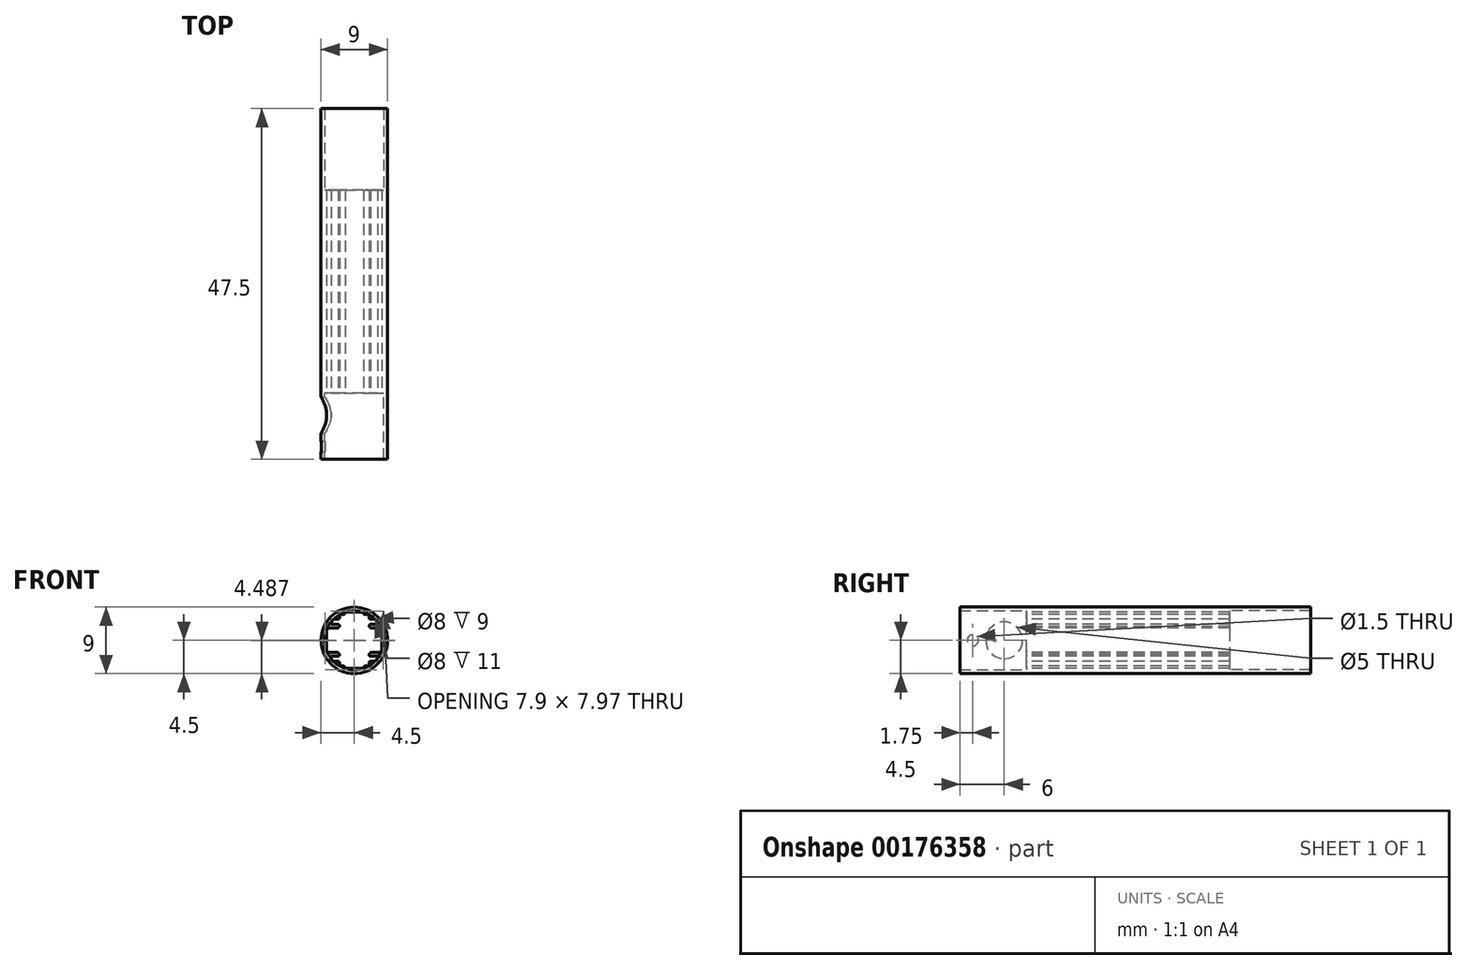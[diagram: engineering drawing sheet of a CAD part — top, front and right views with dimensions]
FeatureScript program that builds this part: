
annotation { "Feature Type Name" : "Feature", "Feature Type Description" : "" }
export const myFeature = defineFeature(function(context is Context, id is Id, definition is map)
    precondition{}
    {
        {
            assignVariable(context, id + "F0", {"name" : "Main_Length", "anyValue" : 47.5});
        }
        {
            assignVariable(context, id + "F1", {"name" : "Bore_Depth_F", "anyValue" : 9});
        }
        {
            assignVariable(context, id + "F2", {"name" : "Bore_Depth_R", "anyValue" : 11});
        }
        {
            var Q0;
            Q0=qCreatedBy(makeId("Front.planeOp"),FACE);
            var sketch = newSketch(context, id + "F3", { "sketchPlane" : qUnion([Q0])});
            skCircle(sketch, "E0", {"center": v(0, 0) * mm, "radius": 4.5 * mm});
            skSolve(sketch);
        }
        {
            var Q0;
            Q0=makeQuery(id+"F3.imprint","IMPRINT",FACE,{"disambiguationData":[TD([[makeQuery(id+"F3.imprint","IMPRINT",EDGE,{"derivedFrom":sQuery(id+"F3.wireOp",EDGE,"E0")}),1.0]])]});
            extrude(context, id + "F4", {"entities" : qUnion([Q0]), "depth" : (getVariable(context, 'Main_Length') - getVariable(context, 'Bore_Depth_F') - getVariable(context, 'Bore_Depth_R')) * mm});
        }
        {
            var Q0;
            Q0=makeQuery(id+"F4.opExtrude","CAP_FACE",FACE,{"disambiguationData":[OSD([sQuery(id+"F3.wireOp",EDGE,"E0")])],"isStart":false});
            var sketch = newSketch(context, id + "F5", { "sketchPlane" : qUnion([Q0])});
            skLineSegment(sketch, "E1", {"start": v(0, -3.8) * mm, "end": v(1.25, -3.8) * mm});
            skLineSegment(sketch, "E2", {"start": v(3.75, -1.65) * mm, "end": v(3.75, 0) * mm});
            skLineSegment(sketch, "E3", {"start": v(1.45, -3.5) * mm, "end": v(2, -3.5) * mm});
            skLineSegment(sketch, "E4", {"start": v(3.15, 2.15) * mm, "end": v(2.2, 2.15) * mm});
            skLineSegment(sketch, "E5", {"start": v(2, -1.95) * mm, "end": v(2, -1.89) * mm});
            skLineSegment(sketch, "E6", {"start": v(1.25, -3.8) * mm, "end": v(1.25, -3.7) * mm});
            skArc(sketch, "E7", {"start": v(2, -1.95) * mm, "mid": v(2.06, -2.1) * mm, "end": v(2.2, -2.15) * mm});
            skArc(sketch, "E8", {"start": v(1.45, -3.5) * mm, "mid": v(1.3, -3.56) * mm, "end": v(1.25, -3.7) * mm});
            skArc(sketch, "E9", {"start": v(2.2, 2.85) * mm, "mid": v(2.06, 2.9) * mm, "end": v(2, 3.05) * mm});
            skArc(sketch, "E10", {"start": v(2, 1.95) * mm, "mid": v(2.06, 2.1) * mm, "end": v(2.2, 2.15) * mm});
            skArc(sketch, "E11", {"start": v(2.2, -2.85) * mm, "mid": v(2.06, -2.9) * mm, "end": v(2, -3.05) * mm});
            skLineSegment(sketch, "E12", {"start": v(1.25, 3.8) * mm, "end": v(1.25, 3.7) * mm});
            skLineSegment(sketch, "E13", {"start": v(-3.75, -1.65) * mm, "end": v(-3.75, 0) * mm});
            skLineSegment(sketch, "E14", {"start": v(-3.15, -2.15) * mm, "end": v(-2.2, -2.15) * mm});
            skLineSegment(sketch, "E15", {"start": v(-3.15, -2.85) * mm, "end": v(-3.15, -2.15) * mm});
            skLineSegment(sketch, "E16", {"start": v(-2.2, -2.85) * mm, "end": v(-3.15, -2.85) * mm});
            skLineSegment(sketch, "E17", {"start": v(-2, -3.5) * mm, "end": v(-2, -3.05) * mm});
            skArc(sketch, "E18", {"start": v(-2.2, -2.85) * mm, "mid": v(-2.06, -2.9) * mm, "end": v(-2, -3.05) * mm});
            skLineSegment(sketch, "E19", {"start": v(-2, -1.95) * mm, "end": v(-2, -1.89) * mm});
            skLineSegment(sketch, "E20", {"start": v(-1.25, -3.8) * mm, "end": v(-1.25, -3.7) * mm});
            skArc(sketch, "E21", {"start": v(-1.45, 3.5) * mm, "mid": v(-1.3, 3.56) * mm, "end": v(-1.25, 3.7) * mm});
            skLineSegment(sketch, "E22", {"start": v(-3.15, 2.15) * mm, "end": v(-2.2, 2.15) * mm});
            skLineSegment(sketch, "E23", {"start": v(2.2, -2.85) * mm, "end": v(3.15, -2.85) * mm});
            skLineSegment(sketch, "E24", {"start": v(2.2, -1.65) * mm, "end": v(3.75, -1.65) * mm});
            skLineSegment(sketch, "E25", {"start": v(-2.2, 2.85) * mm, "end": v(-3.15, 2.85) * mm});
            skLineSegment(sketch, "E26", {"start": v(-1.45, 3.5) * mm, "end": v(-2, 3.5) * mm});
            skLineSegment(sketch, "E27", {"start": v(0, 3.8) * mm, "end": v(-1.25, 3.8) * mm});
            skLineSegment(sketch, "E28", {"start": v(3.15, -2.85) * mm, "end": v(3.15, -2.15) * mm});
            skLineSegment(sketch, "E29", {"start": v(-1.45, -3.5) * mm, "end": v(-2, -3.5) * mm});
            skLineSegment(sketch, "E30", {"start": v(-2, 3.5) * mm, "end": v(-2, 3.05) * mm});
            skArc(sketch, "E31", {"start": v(-1.45, -3.5) * mm, "mid": v(-1.3, -3.56) * mm, "end": v(-1.25, -3.7) * mm});
            skArc(sketch, "E32", {"start": v(-2, 1.95) * mm, "mid": v(-2.06, 2.1) * mm, "end": v(-2.2, 2.15) * mm});
            skArc(sketch, "E33", {"start": v(2, -1.89) * mm, "mid": v(2.1, -1.77) * mm, "end": v(2.2, -1.65) * mm});
            skLineSegment(sketch, "E34", {"start": v(2.2, 1.65) * mm, "end": v(3.75, 1.65) * mm});
            skLineSegment(sketch, "E35", {"start": v(3.15, 2.85) * mm, "end": v(3.15, 2.15) * mm});
            skLineSegment(sketch, "E36", {"start": v(2, -3.5) * mm, "end": v(2, -3.05) * mm});
            skLineSegment(sketch, "E37", {"start": v(-2.2, -1.65) * mm, "end": v(-3.75, -1.65) * mm});
            skLineSegment(sketch, "E38", {"start": v(-3.75, 1.65) * mm, "end": v(-3.75, 0) * mm});
            skLineSegment(sketch, "E39", {"start": v(0, -3.8) * mm, "end": v(-1.25, -3.8) * mm});
            skLineSegment(sketch, "E40", {"start": v(2, 1.95) * mm, "end": v(2, 1.89) * mm});
            skLineSegment(sketch, "E41", {"start": v(-3.15, 2.85) * mm, "end": v(-3.15, 2.15) * mm});
            skLineSegment(sketch, "E42", {"start": v(0, 3.8) * mm, "end": v(1.25, 3.8) * mm});
            skLineSegment(sketch, "E43", {"start": v(3.15, -2.15) * mm, "end": v(2.2, -2.15) * mm});
            skLineSegment(sketch, "E44", {"start": v(-2.2, 1.65) * mm, "end": v(-3.75, 1.65) * mm});
            skLineSegment(sketch, "E45", {"start": v(-1.25, 3.8) * mm, "end": v(-1.25, 3.7) * mm});
            skArc(sketch, "E46", {"start": v(-2, -1.95) * mm, "mid": v(-2.06, -2.1) * mm, "end": v(-2.2, -2.15) * mm});
            skArc(sketch, "E47", {"start": v(2.2, 1.65) * mm, "mid": v(2.1, 1.77) * mm, "end": v(2, 1.89) * mm});
            skArc(sketch, "E48", {"start": v(-2.2, 2.85) * mm, "mid": v(-2.06, 2.9) * mm, "end": v(-2, 3.05) * mm});
            skLineSegment(sketch, "E49", {"start": v(-2, 1.95) * mm, "end": v(-2, 1.89) * mm});
            skArc(sketch, "E50", {"start": v(1.45, 3.5) * mm, "mid": v(1.3, 3.56) * mm, "end": v(1.25, 3.7) * mm});
            skLineSegment(sketch, "E51", {"start": v(3.75, 1.65) * mm, "end": v(3.75, 0) * mm});
            skLineSegment(sketch, "E52", {"start": v(1.45, 3.5) * mm, "end": v(2, 3.5) * mm});
            skLineSegment(sketch, "E53", {"start": v(2.2, 2.85) * mm, "end": v(3.15, 2.85) * mm});
            skLineSegment(sketch, "E54", {"start": v(2, 3.5) * mm, "end": v(2, 3.05) * mm});
            skArc(sketch, "E55", {"start": v(-2.2, -1.65) * mm, "mid": v(-2.1, -1.77) * mm, "end": v(-2, -1.89) * mm});
            skArc(sketch, "E56", {"start": v(-2, 1.89) * mm, "mid": v(-2.1, 1.77) * mm, "end": v(-2.2, 1.65) * mm});
            skSolve(sketch);
        }
        {
            var Q0;
            Q0=makeQuery(id+"F4.opExtrude","CAP_FACE",FACE,{"disambiguationData":[OSD([sQuery(id+"F3.wireOp",EDGE,"E0")])],"isStart":false});
            var sketch = newSketch(context, id + "F6", { "sketchPlane" : qUnion([Q0])});
            skCircle(sketch, "E57.0", {"center": v(0, 0) * mm, "radius": 4.5 * mm});
            skCircle(sketch, "E58", {"center": v(0, 0) * mm, "radius": 4 * mm});
            skSolve(sketch);
        }
        {
            var Q0;
            Q0=makeQuery(id+"F4.opExtrude","CAP_FACE",FACE,{"disambiguationData":[OSD([sQuery(id+"F3.wireOp",EDGE,"E0")])],"isStart":true});
            var sketch = newSketch(context, id + "F7", { "sketchPlane" : qUnion([Q0])});
            skCircle(sketch, "E59.0", {"center": v(0, 0) * mm, "radius": 4.5 * mm});
            skCircle(sketch, "E60", {"center": v(0, 0) * mm, "radius": 4 * mm});
            skSolve(sketch);
        }
        {
            var Q0;
            Q0=makeQuery(id+"F5.imprint","IMPRINT",FACE,{"disambiguationData":[TD([[makeQuery(id+"F5.imprint","IMPRINT",EDGE,{"derivedFrom":sQuery(id+"F5.wireOp",EDGE,"E1")}),1.0]])]});
            extrude(context, id + "F8", {"entities" : qUnion([Q0]), "operationType" : NewBodyOperationType.REMOVE, "endBound" : BoundingType.UP_TO_NEXT, "oppositeDirection" : true, "depth" : 25 * mm});
        }
        {
            var Q0;
            Q0=makeQuery(id+"F6.imprint","IMPRINT",FACE,{"disambiguationData":[TD([[makeQuery(id+"F6.imprint","IMPRINT",EDGE,{"derivedFrom":sQuery(id+"F6.wireOp",EDGE,"E57.0")}),1.0]])]});
            extrude(context, id + "F9", {"entities" : qUnion([Q0]), "operationType" : NewBodyOperationType.ADD, "depth" : (getVariable(context, 'Bore_Depth_F')) * mm});
        }
        {
            var Q0;
            Q0=makeQuery(id+"F7.imprint","IMPRINT",FACE,{"disambiguationData":[TD([[makeQuery(id+"F7.imprint","IMPRINT",EDGE,{"derivedFrom":sQuery(id+"F7.wireOp",EDGE,"E59.0")}),-1.0]])]});
            extrude(context, id + "F10", {"entities" : qUnion([Q0]), "operationType" : NewBodyOperationType.ADD, "depth" : (getVariable(context, 'Bore_Depth_R')) * mm});
        }
        {
            var Q0;
            Q0=qCreatedBy(makeId("Right.planeOp"),FACE);
            var sketch = newSketch(context, id + "F11", { "sketchPlane" : qUnion([Q0])});
            skCircle(sketch, "E61", {"center": v(-30.5, 0) * mm, "radius": 2.5 * mm});
            skCircle(sketch, "E62", {"center": v(-34.75, 0) * mm, "radius": 0.75 * mm});
            skSolve(sketch);
        }
        {
            var Q0;
            Q0=makeQuery(id+"F11.imprint","IMPRINT",FACE,{"disambiguationData":[TD([[makeQuery(id+"F11.imprint","IMPRINT",EDGE,{"derivedFrom":sQuery(id+"F11.wireOp",EDGE,"E61")}),1.0]])]});
            var Q1;
            Q1=makeQuery(id+"F11.imprint","IMPRINT",FACE,{"disambiguationData":[TD([[makeQuery(id+"F11.imprint","IMPRINT",EDGE,{"derivedFrom":sQuery(id+"F11.wireOp",EDGE,"E62")}),1.0]])]});
            extrude(context, id + "F12", {"entities" : qUnion([Q0, Q1]), "operationType" : NewBodyOperationType.REMOVE, "endBound" : BoundingType.THROUGH_ALL, "oppositeDirection" : true, "depth" : 25 * mm});
        }
    });
